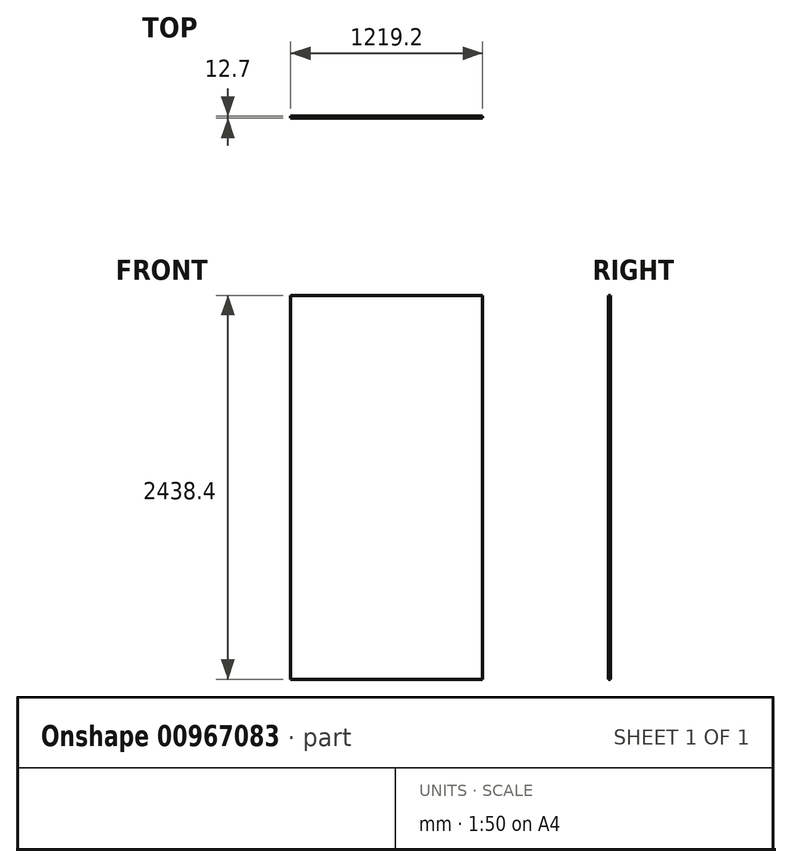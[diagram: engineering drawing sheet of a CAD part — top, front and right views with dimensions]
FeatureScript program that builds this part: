
annotation { "Feature Type Name" : "Feature", "Feature Type Description" : "" }
export const myFeature = defineFeature(function(context is Context, id is Id, definition is map)
    precondition{}
    {
        {
            var Q0;
            Q0=qCreatedBy(makeId("Front.planeOp"),FACE);
            var sketch = newSketch(context, id + "F0", { "sketchPlane" : qUnion([Q0])});
            skLineSegment(sketch, "E0.bottom", {"start": v(0, 0) * mm, "end": v(-1219.2, 0) * mm});
            skLineSegment(sketch, "E0.top", {"start": v(0, 2438.4) * mm, "end": v(-1219.2, 2438.4) * mm});
            skLineSegment(sketch, "E0.left", {"start": v(0, 0) * mm, "end": v(0, 2438.4) * mm});
            skLineSegment(sketch, "E0.right", {"start": v(-1219.2, 0) * mm, "end": v(-1219.2, 2438.4) * mm});
            skSolve(sketch);
        }
        {
            var Q0;
            Q0=makeQuery(id+"F0.imprint","IMPRINT",FACE,{"disambiguationData":[TD([[makeQuery(id+"F0.imprint","IMPRINT",EDGE,{"derivedFrom":sQuery(id+"F0.wireOp",EDGE,"E0.bottom")}),-1.0]])]});
            extrude(context, id + "F1", {"entities" : qUnion([Q0]), "depth" : 12.7 * mm, "offsetDistance" : 25.4 * mm});
        }
    });
